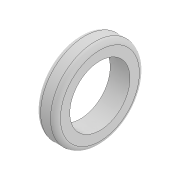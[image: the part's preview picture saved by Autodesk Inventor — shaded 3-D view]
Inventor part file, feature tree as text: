
AUTODESK INVENTOR PART (.ipt)
format: ipt  version: 2022 (Build 260153000, 153)  size: 121,856 bytes
history: native  units: mm
features: extrude x1, fillet x1, thicken_offset x1, sketch x1
ambient origin geometry x8: Origin, YZ Plane, XZ Plane, XY Plane, X Axis, Y Axis, Z Axis, Center Point
bodies: Solid1 (feature_tree)
feature tree (4):
  extrude  "Extrusion1"  Depth=0.5mm
  fillet  "Fillet1"  Radius=2.0mm
  thicken_offset  "Thicken4"
  sketch  "Sketch1"  dims[d0=5.7mm d1=9.0mm d2=2.0mm d3=0.0mm d10=0.5mm d15=0.2mm d16=0.15mm]
